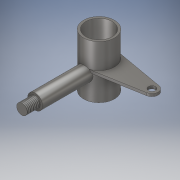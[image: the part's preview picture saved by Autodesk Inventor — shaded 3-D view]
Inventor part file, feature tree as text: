
AUTODESK INVENTOR PART (.ipt)
format: ipt  version: 2019 (Build 230136000, 136)  size: 192,000 bytes
history: native  units: mm
features: extrude x5, sketch x4, plane x3, projected_geometry x2, thread x1
ambient origin geometry x8: Origin, YZ Plane, XZ Plane, XY Plane, X Axis, Y Axis, Z Axis, Center Point
bodies: Solid1 (feature_tree)
feature tree (15):
  extrude  "Extrusion1"  Depth=30.0mm
  plane  "Work Plane4"
  sketch  "Sketch2"  dims[d2=60.0mm d3=0.0mm d4=17.5mm]
  extrude  "Extrusion2"  Depth=17.5mm
  extrude  "Extrusion3"  Depth=25.0mm
  extrude  "Extrusion4"  Depth=3.0mm TaperAngle=0.0deg
  thread  "Thread1"  [1 undecoded]
  plane  "Work Plane5"
  plane  "Work Plane6"
  extrude  "Extrusion5"  Depth=3.0mm TaperAngle=0.0deg
  sketch  "Sketch1"  dims[d0=35.0mm d1=30.0mm]
  projected_geometry  "Projected Loop1"
  sketch  "Sketch3"  dims[d5=17.0mm d6=25.0mm]
  projected_geometry  "Projected Loop2"
  sketch  "Sketch7"  dims[d7=55.0mm d8=0.0mm d9=70.0mm d10=0.0mm d11=12.0mm d12=15.0mm d13=0.0mm d14=15.0mm d15=0.0mm d23=9.599311mm d35=14.0mm d36=60.0mm d37=8.0mm d38=3.0mm d39=0.0mm]
note: 1 required parameter value undecoded (feature->parameter linkage not recoverable at this tier; creation-order binding heuristic only, values carry confidence <= 0.55)
